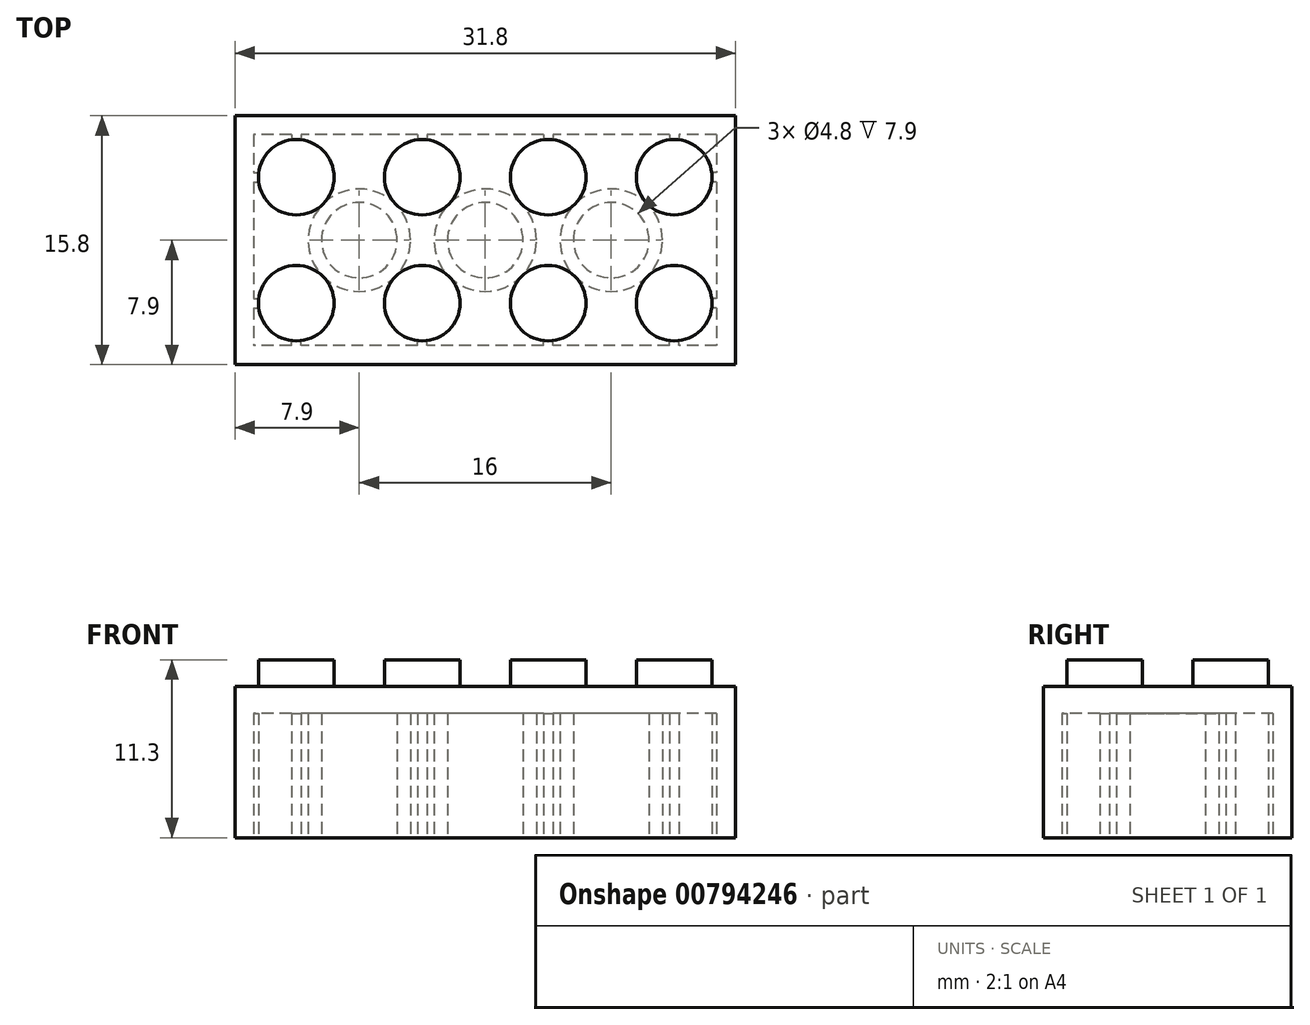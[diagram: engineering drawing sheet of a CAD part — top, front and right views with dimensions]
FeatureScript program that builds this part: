
annotation { "Feature Type Name" : "Feature", "Feature Type Description" : "" }
export const myFeature = defineFeature(function(context is Context, id is Id, definition is map)
    precondition{}
    {
        {
            var Q0;
            Q0=qCreatedBy(makeId("Top.planeOp"),FACE);
            var sketch = newSketch(context, id + "F0", { "sketchPlane" : qUnion([Q0])});
            skLineSegment(sketch, "E0.bottom", {"start": v(-15.9, 7.9) * mm, "end": v(15.9, 7.9) * mm});
            skLineSegment(sketch, "E0.top", {"start": v(-15.9, -7.9) * mm, "end": v(15.9, -7.9) * mm});
            skLineSegment(sketch, "E0.left", {"start": v(-15.9, 7.9) * mm, "end": v(-15.9, -7.9) * mm});
            skLineSegment(sketch, "E0.right", {"start": v(15.9, 7.9) * mm, "end": v(15.9, -7.9) * mm});
            skLineSegment(sketch, "E1.bottom", {"start": v(14.7, 6.7) * mm, "end": v(-14.7, 6.7) * mm});
            skLineSegment(sketch, "E1.top", {"start": v(14.7, -6.7) * mm, "end": v(-14.7, -6.7) * mm});
            skLineSegment(sketch, "E1.left", {"start": v(14.7, 6.7) * mm, "end": v(14.7, -6.7) * mm});
            skLineSegment(sketch, "E1.right", {"start": v(-14.7, 6.7) * mm, "end": v(-14.7, -6.7) * mm});
            skCircle(sketch, "E2", {"center": v(-8, 0) * mm, "radius": 2.4 * mm});
            skCircle(sketch, "E3", {"center": v(-8, 0) * mm, "radius": 3.25 * mm});
            skCircle(sketch, "E4.1.0.0", {"center": v(0, 0) * mm, "radius": 3.25 * mm});
            skCircle(sketch, "E4.1.0.1", {"center": v(0, 0) * mm, "radius": 2.4 * mm});
            skCircle(sketch, "E4.2.0.0", {"center": v(8, 0) * mm, "radius": 3.25 * mm});
            skCircle(sketch, "E4.2.0.1", {"center": v(8, 0) * mm, "radius": 2.4 * mm});
            skLineSegment(sketch, "E4.direction1", {"start": v(-8, 0) * mm, "end": v(0, 0) * mm, "construction": true});
            skLineSegment(sketch, "E5", {"start": v(-12, 14.84) * mm, "end": v(-12, -19) * mm, "construction": true});
            skLineSegment(sketch, "E6", {"start": v(-4, 14.25) * mm, "end": v(-4, -19.71) * mm, "construction": true});
            skLineSegment(sketch, "E7", {"start": v(4, 14.78) * mm, "end": v(4, -19.84) * mm, "construction": true});
            skLineSegment(sketch, "E8", {"start": v(12, 14.65) * mm, "end": v(12, -17.95) * mm, "construction": true});
            skLineSegment(sketch, "E9", {"start": v(-23.95, 4) * mm, "end": v(28.14, 4) * mm, "construction": true});
            skLineSegment(sketch, "E10", {"start": v(-24.54, -4) * mm, "end": v(28.34, -4) * mm, "construction": true});
            skSolve(sketch);
        }
        {
            var Q0;
            Q0=makeQuery(id+"F0.imprint","IMPRINT",FACE,{"disambiguationData":[TD([[makeQuery(id+"F0.imprint","IMPRINT",EDGE,{"derivedFrom":sQuery(id+"F0.wireOp",EDGE,"E0.bottom")}),-1.0]])]});
            var Q1;
            Q1=makeQuery(id+"F0.imprint","IMPRINT",FACE,{"disambiguationData":[TD([[makeQuery(id+"F0.imprint","IMPRINT",EDGE,{"derivedFrom":sQuery(id+"F0.wireOp",EDGE,"E1.bottom")}),1.0]])]});
            var Q2;
            Q2=makeQuery(id+"F0.imprint","IMPRINT",FACE,{"disambiguationData":[TD([[makeQuery(id+"F0.imprint","IMPRINT",EDGE,{"derivedFrom":sQuery(id+"F0.wireOp",EDGE,"E2")}),1.0]])]});
            var Q3;
            Q3=makeQuery(id+"F0.imprint","IMPRINT",FACE,{"disambiguationData":[TD([[makeQuery(id+"F0.imprint","IMPRINT",EDGE,{"derivedFrom":sQuery(id+"F0.wireOp",EDGE,"E4.1.0.1")}),1.0]])]});
            var Q4;
            Q4=makeQuery(id+"F0.imprint","IMPRINT",FACE,{"disambiguationData":[TD([[makeQuery(id+"F0.imprint","IMPRINT",EDGE,{"derivedFrom":sQuery(id+"F0.wireOp",EDGE,"E4.2.0.1")}),1.0]])]});
            var Q5;
            Q5=makeQuery(id+"F0.imprint","IMPRINT",FACE,{"disambiguationData":[TD([[makeQuery(id+"F0.imprint","IMPRINT",EDGE,{"derivedFrom":sQuery(id+"F0.wireOp",EDGE,"E2")}),-1.0]])]});
            var Q6;
            Q6=makeQuery(id+"F0.imprint","IMPRINT",FACE,{"disambiguationData":[TD([[makeQuery(id+"F0.imprint","IMPRINT",EDGE,{"derivedFrom":sQuery(id+"F0.wireOp",EDGE,"E4.1.0.0")}),1.0]])]});
            var Q7;
            Q7=makeQuery(id+"F0.imprint","IMPRINT",FACE,{"disambiguationData":[TD([[makeQuery(id+"F0.imprint","IMPRINT",EDGE,{"derivedFrom":sQuery(id+"F0.wireOp",EDGE,"E4.2.0.0")}),1.0]])]});
            var Q8;
            Q8=makeQuery(id+"F0.imprint","IMPRINT",FACE,{"disambiguationData":[TD([[makeQuery(id+"F0.imprint","IMPRINT",EDGE,{"derivedFrom":sQuery(id+"F0.wireOp",EDGE,"AsDnRDio-Svdu-MVl4-9ALq-DVnELwKl1ONe.bottom")}),-1.0]])]});
            var Q9;
            Q9=makeQuery(id+"F0.imprint","IMPRINT",FACE,{"disambiguationData":[TD([[makeQuery(id+"F0.imprint","IMPRINT",EDGE,{"derivedFrom":sQuery(id+"F0.wireOp",EDGE,"afdb91ba-f5b5-4d7f-b1f4-c6813072fb87.1.0.0")}),-1.0]])]});
            var Q10;
            Q10=makeQuery(id+"F0.imprint","IMPRINT",FACE,{"disambiguationData":[TD([[makeQuery(id+"F0.imprint","IMPRINT",EDGE,{"derivedFrom":sQuery(id+"F0.wireOp",EDGE,"afdb91ba-f5b5-4d7f-b1f4-c6813072fb87.2.0.0")}),-1.0]])]});
            var Q11;
            Q11=makeQuery(id+"F0.imprint","IMPRINT",FACE,{"disambiguationData":[TD([[makeQuery(id+"F0.imprint","IMPRINT",EDGE,{"derivedFrom":sQuery(id+"F0.wireOp",EDGE,"afdb91ba-f5b5-4d7f-b1f4-c6813072fb87.3.0.0")}),-1.0]])]});
            var Q12;
            Q12=makeQuery(id+"F0.imprint","IMPRINT",FACE,{"disambiguationData":[TD([[makeQuery(id+"F0.imprint","IMPRINT",EDGE,{"derivedFrom":sQuery(id+"F0.wireOp",EDGE,"afdb91ba-f5b5-4d7f-b1f4-c6813072fb87.3.1.0")}),-1.0]])]});
            var Q13;
            Q13=makeQuery(id+"F0.imprint","IMPRINT",FACE,{"disambiguationData":[TD([[makeQuery(id+"F0.imprint","IMPRINT",EDGE,{"derivedFrom":sQuery(id+"F0.wireOp",EDGE,"afdb91ba-f5b5-4d7f-b1f4-c6813072fb87.2.1.0")}),-1.0]])]});
            var Q14;
            Q14=makeQuery(id+"F0.imprint","IMPRINT",FACE,{"disambiguationData":[TD([[makeQuery(id+"F0.imprint","IMPRINT",EDGE,{"derivedFrom":sQuery(id+"F0.wireOp",EDGE,"afdb91ba-f5b5-4d7f-b1f4-c6813072fb87.1.1.0")}),-1.0]])]});
            var Q15;
            Q15=makeQuery(id+"F0.imprint","IMPRINT",FACE,{"disambiguationData":[TD([[makeQuery(id+"F0.imprint","IMPRINT",EDGE,{"derivedFrom":sQuery(id+"F0.wireOp",EDGE,"afdb91ba-f5b5-4d7f-b1f4-c6813072fb87.0.1.0")}),-1.0]])]});
            extrude(context, id + "F1", {"entities" : qUnion([Q0, Q1, Q2, Q3, Q4, Q5, Q6, Q7, Q8, Q9, Q10, Q11, Q12, Q13, Q14, Q15]), "depth" : 9.6 * mm, "offsetDistance" : 25 * mm});
        }
        {
            var Q0;
            Q0=makeQuery(id+"F0.imprint","IMPRINT",FACE,{"disambiguationData":[TD([[makeQuery(id+"F0.imprint","IMPRINT",EDGE,{"derivedFrom":sQuery(id+"F0.wireOp",EDGE,"E2")}),1.0]])]});
            var Q1;
            Q1=makeQuery(id+"F0.imprint","IMPRINT",FACE,{"disambiguationData":[TD([[makeQuery(id+"F0.imprint","IMPRINT",EDGE,{"derivedFrom":sQuery(id+"F0.wireOp",EDGE,"E4.2.0.1")}),1.0]])]});
            var Q2;
            Q2=makeQuery(id+"F0.imprint","IMPRINT",FACE,{"disambiguationData":[TD([[makeQuery(id+"F0.imprint","IMPRINT",EDGE,{"derivedFrom":sQuery(id+"F0.wireOp",EDGE,"E4.1.0.1")}),1.0]])]});
            var Q3;
            Q3=makeQuery(id+"F0.imprint","IMPRINT",FACE,{"disambiguationData":[TD([[makeQuery(id+"F0.imprint","IMPRINT",EDGE,{"derivedFrom":sQuery(id+"F0.wireOp",EDGE,"E1.bottom")}),1.0]])]});
            extrude(context, id + "F2", {"entities" : qUnion([Q0, Q1, Q2, Q3]), "operationType" : NewBodyOperationType.REMOVE, "depth" : (9.6 - 1.7) * mm, "offsetDistance" : 25 * mm});
        }
        {
            var Q0;
            Q0=makeQuery(id+"F1.opExtrude","CAP_FACE",FACE,{"disambiguationData":[OSD([sQuery(id+"F0.wireOp",EDGE,"E0.bottom"),sQuery(id+"F0.wireOp",EDGE,"E0.top"),sQuery(id+"F0.wireOp",EDGE,"E0.left"),sQuery(id+"F0.wireOp",EDGE,"E0.right")])],"isStart":false});
            var sketch = newSketch(context, id + "F3", { "sketchPlane" : qUnion([Q0])});
            skCircle(sketch, "E11", {"center": v(-12, 4) * mm, "radius": 2.4 * mm});
            skCircle(sketch, "E12.0.1.0", {"center": v(-12, -4) * mm, "radius": 2.4 * mm});
            skCircle(sketch, "E12.1.0.0", {"center": v(-4, 4) * mm, "radius": 2.4 * mm});
            skCircle(sketch, "E12.1.1.0", {"center": v(-4, -4) * mm, "radius": 2.4 * mm});
            skLineSegment(sketch, "E12.direction1", {"start": v(-12, 4) * mm, "end": v(-4, 4) * mm, "construction": true});
            skLineSegment(sketch, "E12.direction2", {"start": v(-12, 4) * mm, "end": v(-12, -4) * mm, "construction": true});
            skCircle(sketch, "E13.0.2.0", {"center": v(4, 4) * mm, "radius": 2.4 * mm});
            skCircle(sketch, "E13.0.2.1", {"center": v(4, -4) * mm, "radius": 2.4 * mm});
            skCircle(sketch, "E13.0.3.0", {"center": v(12, 4) * mm, "radius": 2.4 * mm});
            skCircle(sketch, "E13.0.3.1", {"center": v(12, -4) * mm, "radius": 2.4 * mm});
            skSolve(sketch);
        }
        {
            var Q0;
            Q0 = qSketchRegion(id + "F3", true);
            extrude(context, id + "F4", {"entities" : qUnion([Q0]), "operationType" : NewBodyOperationType.ADD, "depth" : 1.7 * mm, "offsetDistance" : 25 * mm});
        }
        {
            var Q0;
            Q0=qCreatedBy(makeId("Top.planeOp"),FACE);
            var sketch = newSketch(context, id + "F5", { "sketchPlane" : qUnion([Q0])});
            skLineSegment(sketch, "E14.bottom", {"start": v(-12.3, -6.7) * mm, "end": v(-11.7, -6.7) * mm});
            skLineSegment(sketch, "E14.top", {"start": v(-12.3, -6.4) * mm, "end": v(-11.7, -6.4) * mm});
            skLineSegment(sketch, "E14.left", {"start": v(-12.3, -6.7) * mm, "end": v(-12.3, -6.4) * mm});
            skLineSegment(sketch, "E14.right", {"start": v(-11.7, -6.7) * mm, "end": v(-11.7, -6.4) * mm});
            skLineSegment(sketch, "E15", {"start": v(-8, 14.1) * mm, "end": v(-8, -12.78) * mm, "construction": true});
            skLineSegment(sketch, "E16.MirrorCS", {"start": v(-3.7, -6.7) * mm, "end": v(-4.3, -6.7) * mm});
            skLineSegment(sketch, "E17.MirrorCS", {"start": v(-3.7, -6.4) * mm, "end": v(-4.3, -6.4) * mm});
            skLineSegment(sketch, "E18.MirrorCS", {"start": v(-3.7, -6.7) * mm, "end": v(-3.7, -6.4) * mm});
            skLineSegment(sketch, "E19.MirrorCS", {"start": v(-4.3, -6.7) * mm, "end": v(-4.3, -6.4) * mm});
            skLineSegment(sketch, "E20", {"start": v(-16.63, -8.63) * mm, "end": v(-7.46, 0.54) * mm, "construction": true});
            skLineSegment(sketch, "E21.MirrorCS", {"start": v(-14.7, -3.7) * mm, "end": v(-14.4, -3.7) * mm});
            skLineSegment(sketch, "E22.MirrorCS", {"start": v(-14.7, -4.3) * mm, "end": v(-14.7, -3.7) * mm});
            skLineSegment(sketch, "E23.MirrorCS", {"start": v(-14.7, -4.3) * mm, "end": v(-14.4, -4.3) * mm});
            skLineSegment(sketch, "E24.MirrorCS", {"start": v(-14.4, -4.3) * mm, "end": v(-14.4, -3.7) * mm});
            skLineSegment(sketch, "E25.MirrorCS", {"start": v(3.7, -6.4) * mm, "end": v(4.3, -6.4) * mm});
            skLineSegment(sketch, "E26.MirrorCS", {"start": v(12.3, -6.7) * mm, "end": v(12.3, -6.4) * mm});
            skLineSegment(sketch, "E27.MirrorCS", {"start": v(11.7, -6.7) * mm, "end": v(11.7, -6.4) * mm});
            skLineSegment(sketch, "E28.MirrorCS", {"start": v(12.3, -6.7) * mm, "end": v(11.7, -6.7) * mm});
            skLineSegment(sketch, "E29.MirrorCS", {"start": v(4.3, -6.7) * mm, "end": v(4.3, -6.4) * mm});
            skLineSegment(sketch, "E30.MirrorCS", {"start": v(12.3, -6.4) * mm, "end": v(11.7, -6.4) * mm});
            skLineSegment(sketch, "E31.MirrorCS", {"start": v(3.7, -6.7) * mm, "end": v(3.7, -6.4) * mm});
            skLineSegment(sketch, "E32.MirrorCS", {"start": v(14.7, -4.3) * mm, "end": v(14.7, -3.7) * mm});
            skLineSegment(sketch, "E33.MirrorCS", {"start": v(14.7, -3.7) * mm, "end": v(14.4, -3.7) * mm});
            skLineSegment(sketch, "E34.MirrorCS", {"start": v(14.4, -4.3) * mm, "end": v(14.4, -3.7) * mm});
            skLineSegment(sketch, "E35.MirrorCS", {"start": v(3.7, -6.7) * mm, "end": v(4.3, -6.7) * mm});
            skLineSegment(sketch, "E36.MirrorCS", {"start": v(14.7, -4.3) * mm, "end": v(14.4, -4.3) * mm});
            skLineSegment(sketch, "E37.MirrorCS", {"start": v(-3.7, 6.7) * mm, "end": v(-4.3, 6.7) * mm});
            skLineSegment(sketch, "E38.MirrorCS", {"start": v(14.7, 3.7) * mm, "end": v(14.4, 3.7) * mm});
            skLineSegment(sketch, "E39.MirrorCS", {"start": v(11.7, 6.7) * mm, "end": v(11.7, 6.4) * mm});
            skLineSegment(sketch, "E40.MirrorCS", {"start": v(14.7, 4.3) * mm, "end": v(14.7, 3.7) * mm});
            skLineSegment(sketch, "E41.MirrorCS", {"start": v(-12.3, 6.7) * mm, "end": v(-11.7, 6.7) * mm});
            skLineSegment(sketch, "E42.MirrorCS", {"start": v(-4.3, 6.7) * mm, "end": v(-4.3, 6.4) * mm});
            skLineSegment(sketch, "E43.MirrorCS", {"start": v(12.3, 6.4) * mm, "end": v(11.7, 6.4) * mm});
            skLineSegment(sketch, "E44.MirrorCS", {"start": v(-3.7, 6.4) * mm, "end": v(-4.3, 6.4) * mm});
            skLineSegment(sketch, "E45.MirrorCS", {"start": v(12.3, 6.7) * mm, "end": v(11.7, 6.7) * mm});
            skLineSegment(sketch, "E46.MirrorCS", {"start": v(-14.7, 4.3) * mm, "end": v(-14.7, 3.7) * mm});
            skLineSegment(sketch, "E47.MirrorCS", {"start": v(-14.7, 4.3) * mm, "end": v(-14.4, 4.3) * mm});
            skLineSegment(sketch, "E48.MirrorCS", {"start": v(14.7, 4.3) * mm, "end": v(14.4, 4.3) * mm});
            skLineSegment(sketch, "E49.MirrorCS", {"start": v(14.4, 4.3) * mm, "end": v(14.4, 3.7) * mm});
            skLineSegment(sketch, "E50.MirrorCS", {"start": v(3.7, 6.4) * mm, "end": v(4.3, 6.4) * mm});
            skLineSegment(sketch, "E51.MirrorCS", {"start": v(-3.7, 6.7) * mm, "end": v(-3.7, 6.4) * mm});
            skLineSegment(sketch, "E52.MirrorCS", {"start": v(-14.7, 3.7) * mm, "end": v(-14.4, 3.7) * mm});
            skLineSegment(sketch, "E53.MirrorCS", {"start": v(-12.3, 6.4) * mm, "end": v(-11.7, 6.4) * mm});
            skLineSegment(sketch, "E54.MirrorCS", {"start": v(-14.4, 4.3) * mm, "end": v(-14.4, 3.7) * mm});
            skLineSegment(sketch, "E55.MirrorCS", {"start": v(-11.7, 6.7) * mm, "end": v(-11.7, 6.4) * mm});
            skLineSegment(sketch, "E56.MirrorCS", {"start": v(-12.3, 6.7) * mm, "end": v(-12.3, 6.4) * mm});
            skLineSegment(sketch, "E57.MirrorCS", {"start": v(12.3, 6.7) * mm, "end": v(12.3, 6.4) * mm});
            skLineSegment(sketch, "E58.MirrorCS", {"start": v(4.3, 6.7) * mm, "end": v(4.3, 6.4) * mm});
            skLineSegment(sketch, "E59.MirrorCS", {"start": v(3.7, 6.7) * mm, "end": v(4.3, 6.7) * mm});
            skLineSegment(sketch, "E60.MirrorCS", {"start": v(3.7, 6.7) * mm, "end": v(3.7, 6.4) * mm});
            skSolve(sketch);
        }
        {
            var Q0;
            Q0 = qSketchRegion(id + "F5", true);
            extrude(context, id + "F6", {"entities" : qUnion([Q0]), "operationType" : NewBodyOperationType.ADD, "endBound" : BoundingType.UP_TO_NEXT, "depth" : 25 * mm, "offsetDistance" : 25 * mm});
        }
    });
